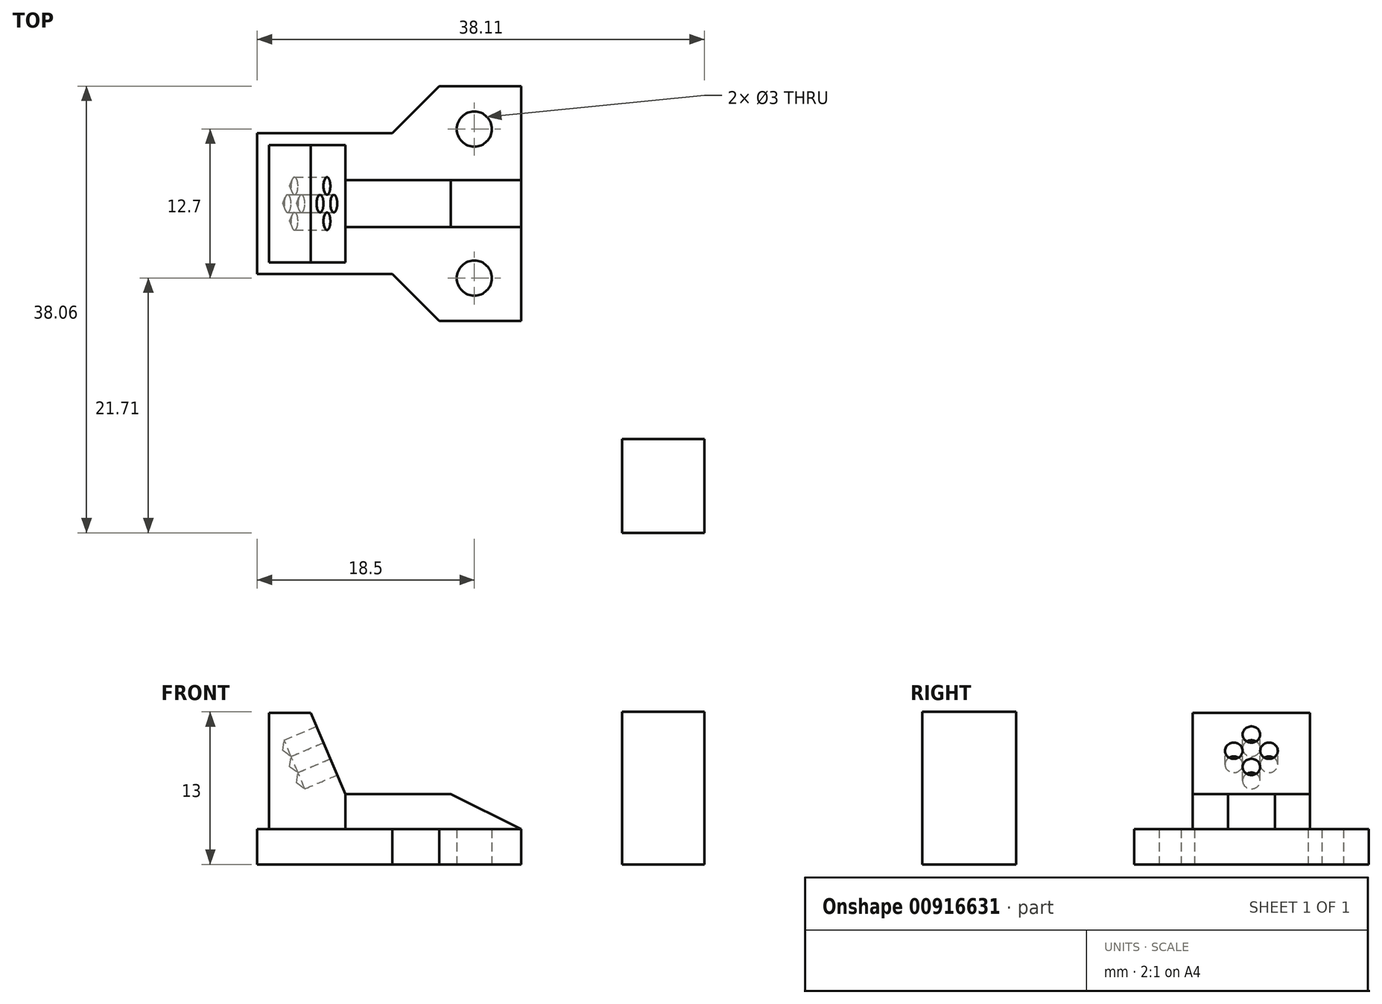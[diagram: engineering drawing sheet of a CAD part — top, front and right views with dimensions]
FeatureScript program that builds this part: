
annotation { "Feature Type Name" : "Feature", "Feature Type Description" : "" }
export const myFeature = defineFeature(function(context is Context, id is Id, definition is map)
    precondition{}
    {
        {
            var Q0;
            Q0=qCreatedBy(makeId("Top.planeOp"),FACE);
            var sketch = newSketch(context, id + "F0", { "sketchPlane" : qUnion([Q0])});
            skCircle(sketch, "E0", {"center": v(0, 6.35) * mm, "radius": 1.5 * mm});
            skLineSegment(sketch, "E1", {"start": v(4, 0) * mm, "end": v(4, 10) * mm});
            skLineSegment(sketch, "E2", {"start": v(4, 10) * mm, "end": v(-3, 10) * mm});
            skLineSegment(sketch, "E3", {"start": v(-3, 10) * mm, "end": v(-7, 6) * mm});
            skLineSegment(sketch, "E4", {"start": v(-7, 6) * mm, "end": v(-18.5, 6) * mm});
            skLineSegment(sketch, "E5", {"start": v(-18.5, 6) * mm, "end": v(-18.5, 0) * mm});
            skLineSegment(sketch, "E6.MirrorCS", {"start": v(4, -10) * mm, "end": v(-3, -10) * mm});
            skLineSegment(sketch, "E7.MirrorCS", {"start": v(-3, -10) * mm, "end": v(-7, -6) * mm});
            skLineSegment(sketch, "E8.MirrorCS", {"start": v(4, 0) * mm, "end": v(4, -10) * mm});
            skLineSegment(sketch, "E9.MirrorCS", {"start": v(-18.5, -6) * mm, "end": v(-18.5, 0) * mm});
            skLineSegment(sketch, "E10.MirrorCS", {"start": v(-7, -6) * mm, "end": v(-18.5, -6) * mm});
            skCircle(sketch, "E11.MirrorC", {"center": v(0, -6.35) * mm, "radius": 1.5 * mm});
            skLineSegment(sketch, "E12.left", {"start": v(12.61, -20.06) * mm, "end": v(12.61, -28.06) * mm});
            skLineSegment(sketch, "E13", {"start": v(19.61, -20.06) * mm, "end": v(19.61, -28.06) * mm});
            skLineSegment(sketch, "E14", {"start": v(12.61, -20.06) * mm, "end": v(19.61, -20.06) * mm});
            skLineSegment(sketch, "E15", {"start": v(19.61, -28.06) * mm, "end": v(12.61, -28.06) * mm});
            skSolve(sketch);
        }
        {
            var Q0;
            Q0=makeQuery(id+"F0.imprint","IMPRINT",FACE,{"disambiguationData":[TD([[makeQuery(id+"F0.imprint","IMPRINT",EDGE,{"derivedFrom":sQuery(id+"F0.wireOp",EDGE,"E0")}),-1.0]])]});
            extrude(context, id + "F1", {"entities" : qUnion([Q0]), "depth" : 3 * mm, "offsetDistance" : 25 * mm});
        }
        {
            var Q0;
            Q0=qCreatedBy(makeId("Front.planeOp"),FACE);
            var sketch = newSketch(context, id + "F2", { "sketchPlane" : qUnion([Q0])});
            skLineSegment(sketch, "E16", {"start": v(-17.5, 3) * mm, "end": v(-17.5, 12.9) * mm});
            skLineSegment(sketch, "E17", {"start": v(-17.5, 12.9) * mm, "end": v(-13.93, 12.9) * mm});
            skLineSegment(sketch, "E18", {"start": v(-13.93, 12.9) * mm, "end": v(-11, 6) * mm});
            skLineSegment(sketch, "E19", {"start": v(-11, 6) * mm, "end": v(-11, 3) * mm});
            skLineSegment(sketch, "E20", {"start": v(-11, 3) * mm, "end": v(-17.5, 3) * mm});
            skSolve(sketch);
        }
        {
            var Q0;
            Q0=makeQuery(id+"F2.imprint","IMPRINT",FACE,{"disambiguationData":[TD([[makeQuery(id+"F2.imprint","IMPRINT",EDGE,{"derivedFrom":sQuery(id+"F2.wireOp",EDGE,"E16")}),-1.0]])]});
            extrude(context, id + "F3", {"entities" : qUnion([Q0]), "operationType" : NewBodyOperationType.ADD, "depth" : 5 * mm, "offsetDistance" : 25 * mm, "hasSecondDirection" : true, "secondDirectionOppositeDirection" : true, "secondDirectionDepth" : 5 * mm});
        }
        {
            var Q0;
            Q0=makeQuery(id+"F3.opExtrude","SWEPT_FACE",FACE,{"disambiguationData":[OSD([sQuery(id+"F2.wireOp",EDGE,"E18")])]});
            var sketch = newSketch(context, id + "F4", { "sketchPlane" : qUnion([Q0])});
            skPoint(sketch, "E21", {"position": v(0, 15.32) * mm});
            skPoint(sketch, "E22", {"position": v(0, 12.32) * mm});
            skPoint(sketch, "E23", {"position": v(1.5, 13.82) * mm});
            skPoint(sketch, "E24", {"position": v(-1.5, 13.82) * mm});
            skSolve(sketch);
        }
        {
            var Q0;
            Q0=sQuery(id+"F4.wireOp",VERTEX,"E21");
            var Q1;
            Q1=sQuery(id+"F4.wireOp",VERTEX,"E23");
            var Q2;
            Q2=sQuery(id+"F4.wireOp",VERTEX,"E22");
            var Q3;
            Q3=sQuery(id+"F4.wireOp",VERTEX,"E24");
            var Q4;
            Q4=makeQuery(id+"F1.opExtrude","SWEPT_BODY",BODY,{"disambiguationData":[OSD([sQuery(id+"F0.wireOp",EDGE,"E0"),sQuery(id+"F0.wireOp",EDGE,"E1"),sQuery(id+"F0.wireOp",EDGE,"E2"),sQuery(id+"F0.wireOp",EDGE,"E3"),sQuery(id+"F0.wireOp",EDGE,"E4"),sQuery(id+"F0.wireOp",EDGE,"E5"),sQuery(id+"F0.wireOp",EDGE,"E6.MirrorCS"),sQuery(id+"F0.wireOp",EDGE,"E7.MirrorCS"),sQuery(id+"F0.wireOp",EDGE,"E8.MirrorCS"),sQuery(id+"F0.wireOp",EDGE,"E9.MirrorCS"),sQuery(id+"F0.wireOp",EDGE,"E10.MirrorCS"),sQuery(id+"F0.wireOp",EDGE,"E11.MirrorC")])]});
            hole(context, id + "F5", {"style" : HoleStyle.SIMPLE, "endStyle" : HoleEndStyle.BLIND, "holeDiameter" : 1.5 * mm, "majorDiameter" : 5 * mm, "holeDepth" : 3 * mm, "isTappedThrough" : true, "tappedDepth" : 12 * mm, "tapClearance" : 3, "locations" : qUnion([Q0, Q1, Q2, Q3]), "scope" : qUnion([Q4])});
        }
        {
            var Q0;
            Q0=makeQuery(id+"F1.opExtrude","CAP_FACE",FACE,{"disambiguationData":[OSD([sQuery(id+"F0.wireOp",EDGE,"E0"),sQuery(id+"F0.wireOp",EDGE,"E1"),sQuery(id+"F0.wireOp",EDGE,"E2"),sQuery(id+"F0.wireOp",EDGE,"E3"),sQuery(id+"F0.wireOp",EDGE,"E4"),sQuery(id+"F0.wireOp",EDGE,"E5"),sQuery(id+"F0.wireOp",EDGE,"E6.MirrorCS"),sQuery(id+"F0.wireOp",EDGE,"E7.MirrorCS"),sQuery(id+"F0.wireOp",EDGE,"E8.MirrorCS"),sQuery(id+"F0.wireOp",EDGE,"E9.MirrorCS"),sQuery(id+"F0.wireOp",EDGE,"E10.MirrorCS"),sQuery(id+"F0.wireOp",EDGE,"E11.MirrorC")])],"isStart":false});
            var sketch = newSketch(context, id + "F6", { "sketchPlane" : qUnion([Q0])});
            skLineSegment(sketch, "E25", {"start": v(4, 2) * mm, "end": v(-4, 2) * mm});
            skLineSegment(sketch, "E26", {"start": v(4, -2) * mm, "end": v(-4, -2) * mm});
            skLineSegment(sketch, "E27", {"start": v(-4, 2) * mm, "end": v(-11, 2) * mm});
            skLineSegment(sketch, "E28", {"start": v(-4, -2) * mm, "end": v(-11, -2) * mm});
            skSolve(sketch);
        }
        {
            var Q0;
            {var subQ0=sQuery(id+"F6.wireOp",EDGE,"E25");Q0=makeQuery(id+"F6.imprint","IMPRINT",FACE,{"disambiguationData":[TD([[makeQuery(id+"F6.imprint","IMPRINT",EDGE,{"derivedFrom":subQ0}),1.0]])]});}
            extrude(context, id + "F7", {"entities" : qUnion([Q0]), "operationType" : NewBodyOperationType.ADD, "depth" : 3 * mm, "offsetDistance" : 25 * mm});
        }
        {
            var Q0;
            Q0=makeQuery(id+"F7.opExtrude","CAP_EDGE",EDGE,{"disambiguationData":[OSD([sQuery(id+"F0.wireOp",EDGE,"E1"),sQuery(id+"F0.wireOp",EDGE,"E8.MirrorCS")])],"isStart":false});
            chamfer(context, id + "F8", {"entities" : qUnion([Q0]), "chamferType" : ChamferType.TWO_OFFSETS, "width1" : 3 * mm, "oppositeDirection" : false, "width2" : 6 * mm, "tangentPropagation" : true});
        }
        {
            var Q0;
            Q0=makeQuery(id+"F0.imprint","IMPRINT",FACE,{"disambiguationData":[TD([[makeQuery(id+"F0.imprint","IMPRINT",EDGE,{"derivedFrom":sQuery(id+"F0.wireOp",EDGE,"E12.left")}),1.0]])]});
            extrude(context, id + "F9", {"entities" : qUnion([Q0]), "depth" : 13 * mm, "offsetDistance" : 25 * mm});
        }
    });
